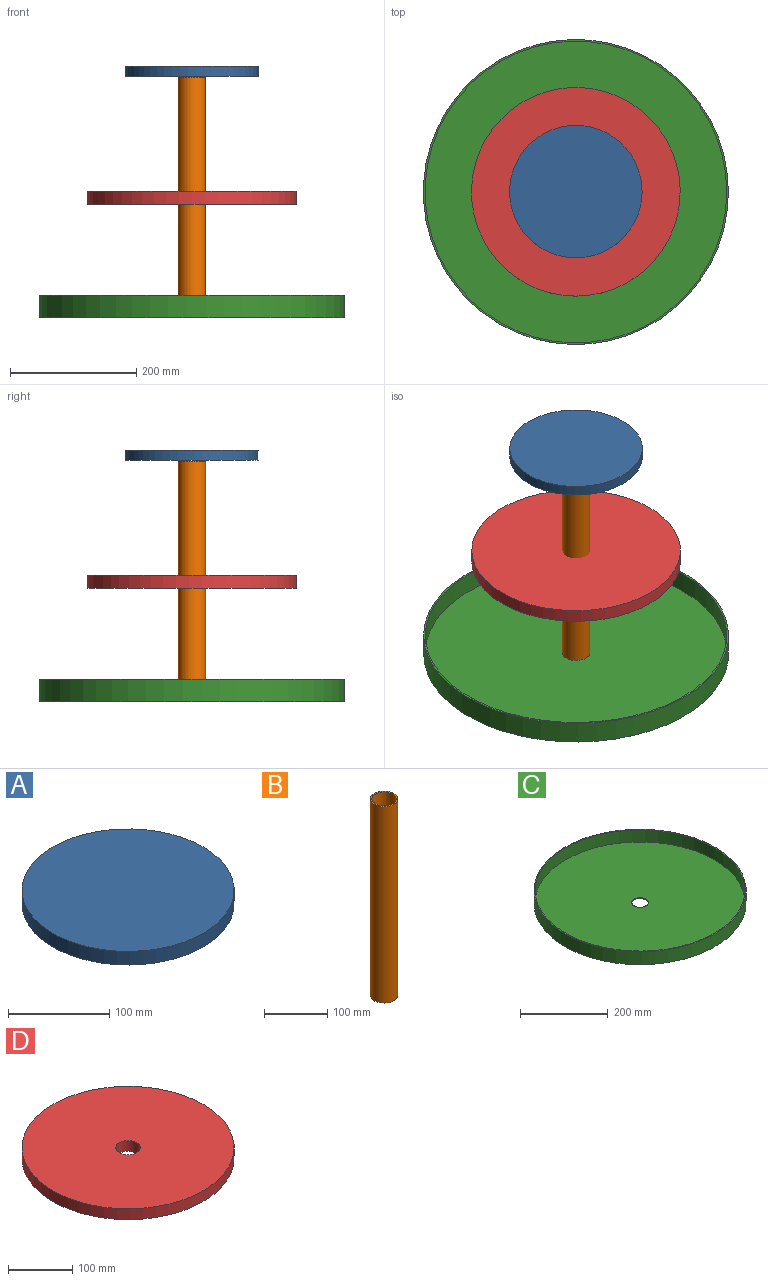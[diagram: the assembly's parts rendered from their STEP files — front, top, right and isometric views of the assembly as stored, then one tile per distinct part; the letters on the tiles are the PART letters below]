
ASSEMBLY  parts=4 mates=3
PART A: 3 faces, bbox 209.7x209.7x16.5 mm
  f0: cylinder r=104.86mm len=209.73mm, axis (0,0,-1), area 10878.2mm2, adj f1,f2
  f1: plane 209.73x209.73mm, normal (0,0,1), area 34546.9mm2, adj f0
  f2: plane 209.73x209.73mm, normal (0,0,-1), area 34546.9mm2, adj f0
PART B: 5 faces, bbox 43.2x43.2x378.5 mm
  f0: cylinder r=21.59mm len=378.46mm, axis (0,0,-1), area 51339.6mm2, adj f1,f2
  f1: plane 43.18x43.18mm, normal (0,0,1), area 324.3mm2, adj f0,f3
  f2: plane 43.18x43.18mm, normal (0,0,-1), area 1464.4mm2, adj f0
  f3: cylinder r=19.05mm len=375.92mm, axis (0,0,-1), area 44995.6mm2, adj f1,f4
  f4: plane 38.1x38.1mm, normal (0,0,1), area 1140.1mm2, adj f3
PART C: 6 faces, bbox 482.6x482.6x36.1 mm
  f0: cylinder r=241.3mm len=482.6mm, axis (0,0,-1), area 54683.9mm2, adj f1,f2
  f1: plane 482.6x482.6mm, normal (0,0,1), area 3830.7mm2, adj f0,f3
  f2: plane 482.6x482.6mm, normal (0,0,-1), area 181781.3mm2, adj f0,f5
  f3: cylinder r=238.76mm len=477.52mm, axis (0,0,-1), area 50297.8mm2, adj f1,f4
  f4: plane 477.52x477.52mm, normal (0,0,1), area 177950.6mm2, adj f3,f5
  f5: cylinder r=19.05mm len=38.1mm, axis (0,0,-1), area 304mm2, adj f2,f4
PART D: 4 faces, bbox 330.2x330.2x20.6 mm
  f0: cylinder r=165.1mm len=330.2mm, axis (0,0,-1), area 21342.5mm2, adj f1,f2
  f1: plane 330.2x330.2mm, normal (0,0,1), area 84493.5mm2, adj f0,f3
  f2: plane 330.2x330.2mm, normal (0,0,-1), area 84493.5mm2, adj f0,f3
  f3: cylinder r=19.05mm len=38.1mm, axis (0,0,-1), area 2462.6mm2, adj f1,f2
PLACE A rot(axis=(0,0,1),90deg) t=(-153.09,-56.44,421.94)mm
PLACE B t=(-153.09,-56.44,44.75)mm
PLACE C t=(-153.09,-56.44,39.67)mm
PLACE D rot(axis=(0,0,-1),90deg) t=(-153.09,-56.44,219.76)mm
MATE slider A.f0 <-> B.f0  axis (0,0,1) through (-153.09,-56.44,438.45)mm
MATE slider D.f0 <-> B.f0  axis (0,0,1) through (-153.09,-56.44,240.33)mm
MATE fastened B.f0 <-> C.f0  axis (0,0,-1) through (-153.09,-56.44,42.21)mm
